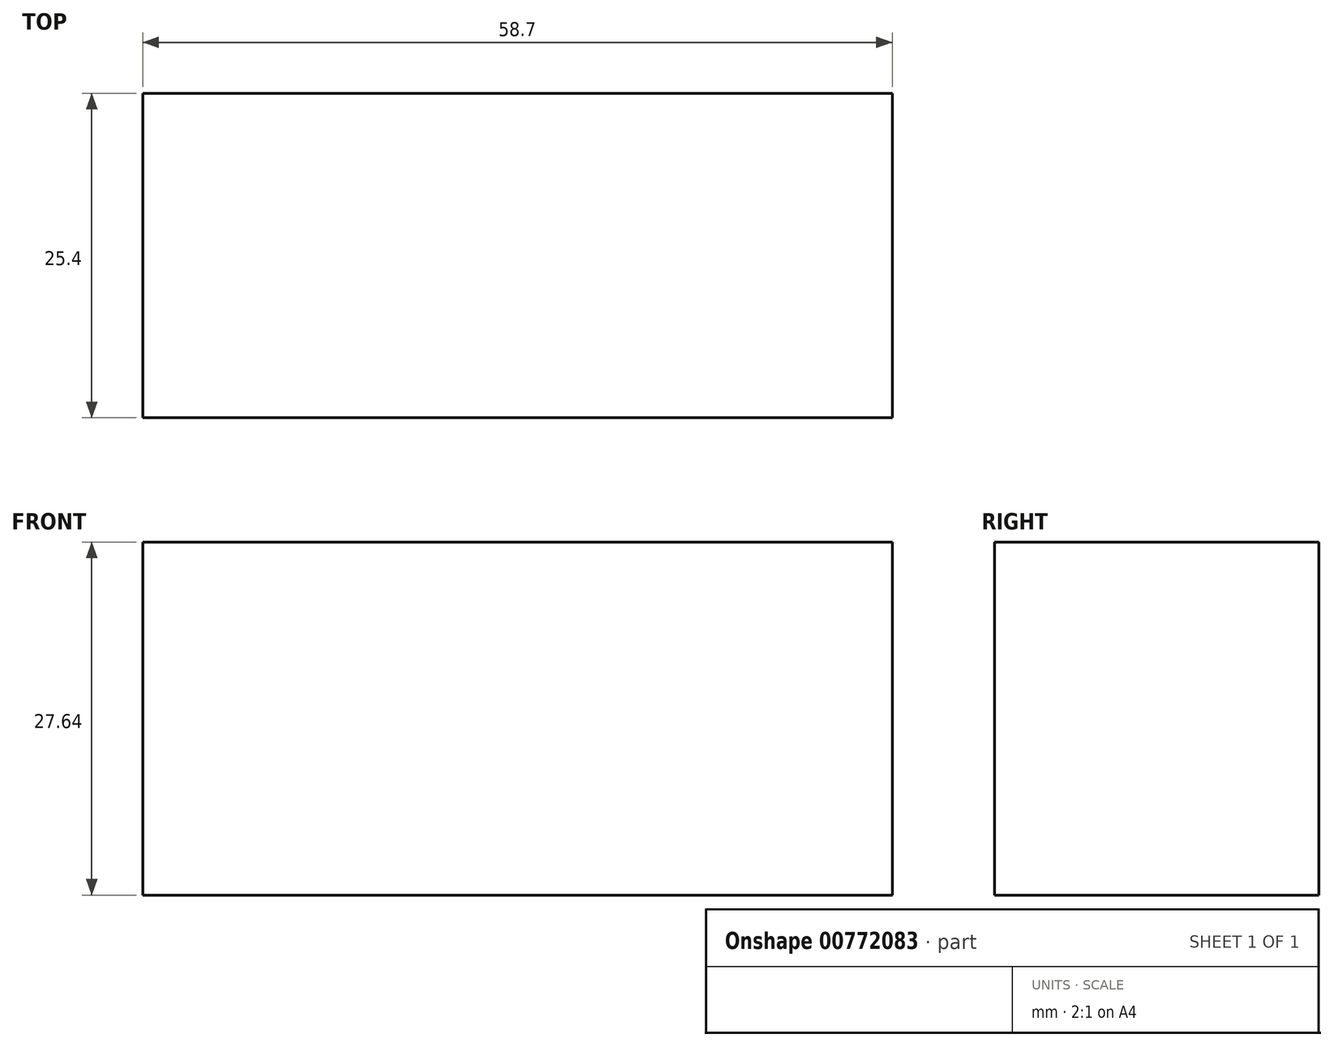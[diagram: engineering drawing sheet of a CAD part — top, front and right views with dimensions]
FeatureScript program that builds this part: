
annotation { "Feature Type Name" : "Feature", "Feature Type Description" : "" }
export const myFeature = defineFeature(function(context is Context, id is Id, definition is map)
    precondition{}
    {
        {
            var Q0;
            Q0=qCreatedBy(makeId("Front.planeOp"),FACE);
            var sketch = newSketch(context, id + "F0", { "sketchPlane" : qUnion([Q0])});
            skLineSegment(sketch, "E0", {"start": v(29.85, 27.64) * mm, "end": v(-28.85, 27.64) * mm});
            skLineSegment(sketch, "E1", {"start": v(-28.85, 27.64) * mm, "end": v(-28.85, 0) * mm});
            skLineSegment(sketch, "E2", {"start": v(29.85, 0) * mm, "end": v(29.85, 27.64) * mm});
            skLineSegment(sketch, "E3", {"start": v(29.85, 0) * mm, "end": v(-28.85, 0) * mm});
            skSolve(sketch);
        }
        {
            var Q0;
            Q0=makeQuery(id+"F0.imprint","IMPRINT",FACE,{"disambiguationData":[TD([[makeQuery(id+"F0.imprint","IMPRINT",EDGE,{"derivedFrom":sQuery(id+"F0.wireOp",EDGE,"E0")}),1.0]])]});
            extrude(context, id + "F1", {"entities" : qUnion([Q0]), "depth" : 25.4 * mm, "offsetDistance" : 25.4 * mm});
        }
    });
